# Revit family: STANDARD 5050 IP55_S2460.U.3_W.3_N.3
name_source: partatom
category: Luminarias
units: mm (PartAtom-declared; Revit-internal decimal feet)

## family parameters
Compartido = No
Corte con vacíos al cargar = No
Cota de conector redondo = Diámetro de uso
Origen de luz = Sí
Punto de cálculo de habitación = No
Se basa en plano de trabajo = Sí
Siempre vertical = No
Tipo de pieza = Normal

## types (3) — shared parameters
Cambio de temperatura de color de luz atenuada = <Ninguno>
Comentarios de vataje = 12
Fabricante = BRILLANT
Filtro de color = 16777215
Longitud de línea de emisión = 600 mm
Marca = BRILLANT
Modelo Lampara = 5050 SMD
Tamaño de símbolo de origen de luz = 610 mm
zero-valued in all types: Elevación por defecto

## per-type parameters (varying)
| type | Descripción | Modelo |
| STANDARD 5050 IP55_S2460.U.3 | TIRA STANDARD 5050 MONOCROMATICA DE PCB BLANCO MONTADA EN UNA CINTA ADHERIBLE 3M CON UNA POTENCIA DE 14.4W/M DE UN TIPO DE LED 5050 SMD, USO PARA INTERIORES IP55, IRC 80, TEMPERATURA EN BLANCO CALIDO 2700K, 1044 LUMENES/M, PRESENTACION DE 5M, CORTE 10CM, ALIMENTADO A 12V, REQUIERE ACCESORIOS. | S2460.U.3 |
| STANDARD 5050 IP55_S2460.W.3 | TIRA STANDARD 5050 MONOCROMATICA DE PCB BLANCO MONTADA EN UNA CINTA ADHERIBLE 3M CON UNA POTENCIA DE 14.4W/M DE UN TIPO DE LED 5050 SMD, USO PARA INTERIORES IP55, IRC 80, TEMPERATURA EN BLANCO CALIDO 3000K, 1101 LUMENES/M, PRESENTACION DE 5M, CORTE 10CM, ALIMENTADO A 12V, REQUIERE ACCESORIOS. | S2460.W.3 |
| STANDARD 5050 IP55_S2460.N.3 | TIRA STANDARD 5050 MONOCROMATICA DE PCB BLANCO MONTADA EN UNA CINTA ADHERIBLE 3M CON UNA POTENCIA DE 14.4W/M DE UN TIPO DE LED 5050 SMD, USO PARA INTERIORES IP55, IRC 80, TEMPERATURA EN BLANCO FRIO 4000K, 1135 LUMENES/M, PRESENTACION DE 5M, CORTE 10CM, ALIMENTADO A 12V, REQUIERE ACCESORIOS. | S2460.N.3 |

## geometry (parser evidence)
native form markers: Blend x2
no freeform markers — native parametric forms only
